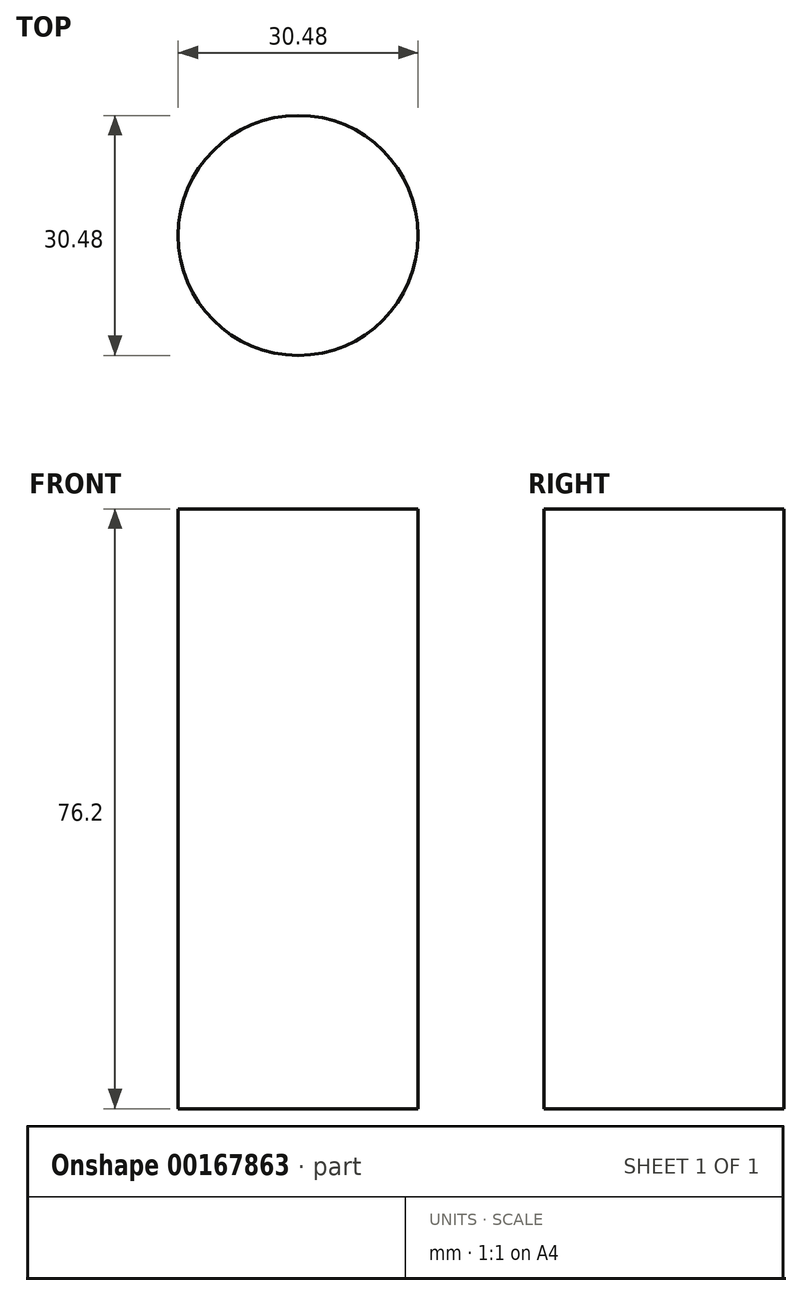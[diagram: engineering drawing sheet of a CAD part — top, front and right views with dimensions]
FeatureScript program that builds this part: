
annotation { "Feature Type Name" : "Feature", "Feature Type Description" : "" }
export const myFeature = defineFeature(function(context is Context, id is Id, definition is map)
    precondition{}
    {
        {
            var Q0;
            Q0=qCreatedBy(makeId("Top.planeOp"),FACE);
            var sketch = newSketch(context, id + "F0", { "sketchPlane" : qUnion([Q0])});
            skCircle(sketch, "E0", {"center": v(0, 0) * mm, "radius": 15.24 * mm});
            skSolve(sketch);
        }
        {
            var Q0;
            Q0 = qSketchRegion(id + "F0", true);
            extrude(context, id + "F1", {"entities" : qUnion([Q0]), "depth" : 76.2 * mm});
        }
    });
